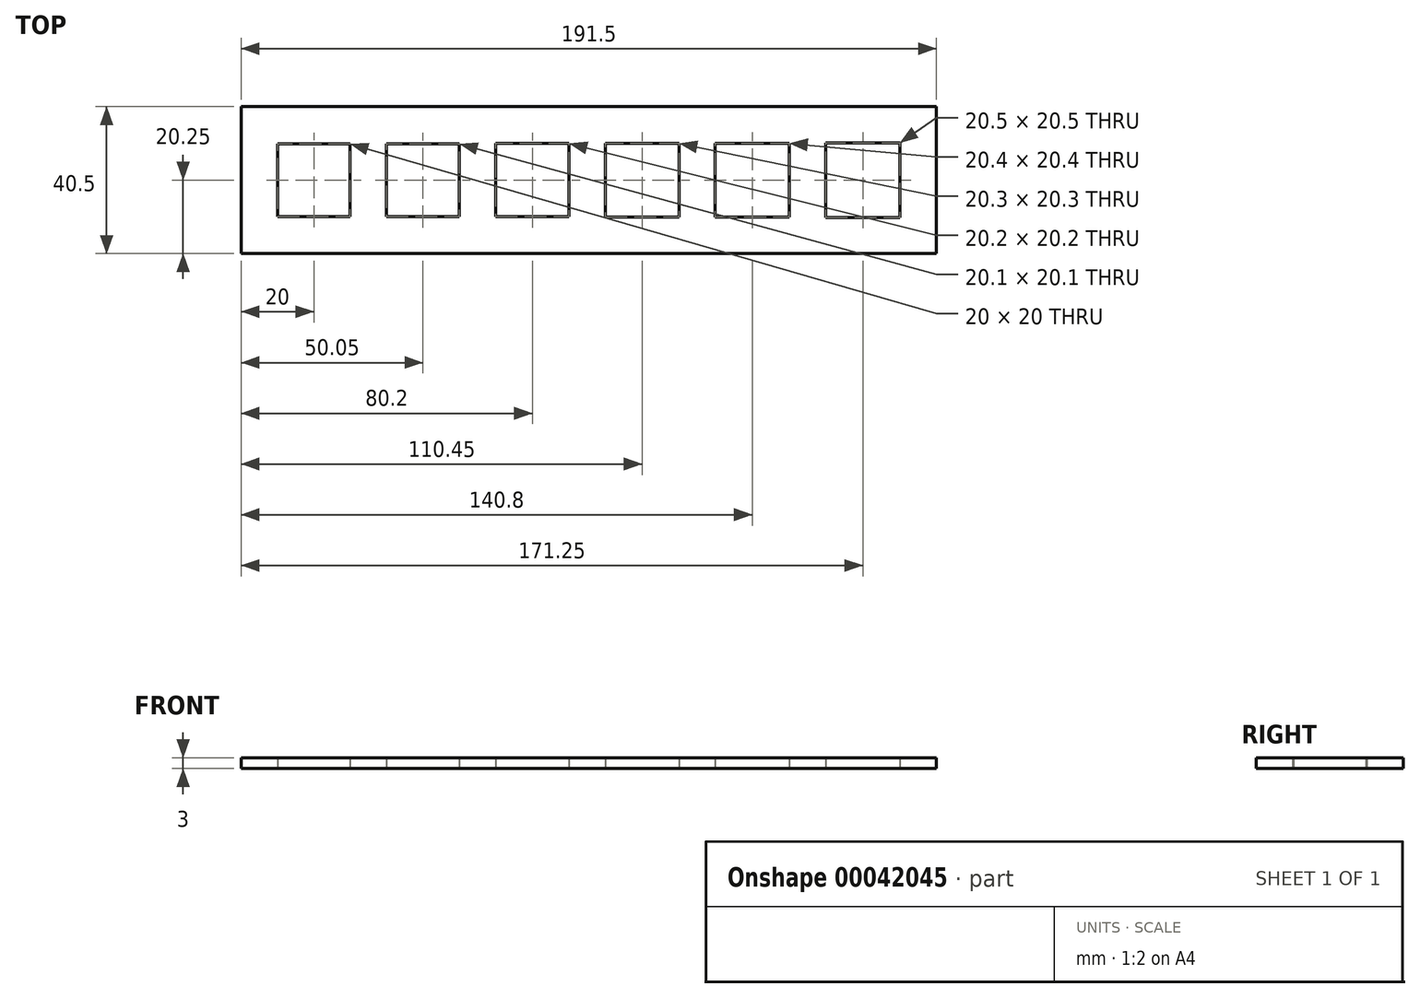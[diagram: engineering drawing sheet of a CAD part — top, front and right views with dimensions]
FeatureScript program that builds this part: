
annotation { "Feature Type Name" : "Feature", "Feature Type Description" : "" }
export const myFeature = defineFeature(function(context is Context, id is Id, definition is map)
    precondition{}
    {
        {
            var Q0;
            Q0=qCreatedBy(makeId("Top.planeOp"),FACE);
            var sketch = newSketch(context, id + "F0", { "sketchPlane" : qUnion([Q0])});
            skLineSegment(sketch, "E0.bottom", {"start": v(-95.75, 20.25) * mm, "end": v(95.75, 20.25) * mm});
            skLineSegment(sketch, "E0.top", {"start": v(-95.75, -20.25) * mm, "end": v(95.75, -20.25) * mm});
            skLineSegment(sketch, "E0.left", {"start": v(-95.75, 20.25) * mm, "end": v(-95.75, -20.25) * mm});
            skLineSegment(sketch, "E0.right", {"start": v(95.75, 20.25) * mm, "end": v(95.75, -20.25) * mm});
            skLineSegment(sketch, "E1.bottom", {"start": v(-85.75, 10) * mm, "end": v(-65.75, 10) * mm});
            skLineSegment(sketch, "E1.top", {"start": v(-85.75, -10) * mm, "end": v(-65.75, -10) * mm});
            skLineSegment(sketch, "E1.left", {"start": v(-85.75, 10) * mm, "end": v(-85.75, -10) * mm});
            skLineSegment(sketch, "E1.right", {"start": v(-65.75, 10) * mm, "end": v(-65.75, -10) * mm});
            skLineSegment(sketch, "E2.bottom", {"start": v(-55.75, 10.05) * mm, "end": v(-35.65, 10.05) * mm});
            skLineSegment(sketch, "E2.top", {"start": v(-55.75, -10.05) * mm, "end": v(-35.65, -10.05) * mm});
            skLineSegment(sketch, "E2.left", {"start": v(-55.75, 10.05) * mm, "end": v(-55.75, -10.05) * mm});
            skLineSegment(sketch, "E2.right", {"start": v(-35.65, 10.05) * mm, "end": v(-35.65, -10.05) * mm});
            skLineSegment(sketch, "E3.bottom", {"start": v(-25.65, 10.1) * mm, "end": v(-5.45, 10.1) * mm});
            skLineSegment(sketch, "E3.top", {"start": v(-25.65, -10.1) * mm, "end": v(-5.45, -10.1) * mm});
            skLineSegment(sketch, "E3.left", {"start": v(-25.65, 10.1) * mm, "end": v(-25.65, -10.1) * mm});
            skLineSegment(sketch, "E3.right", {"start": v(-5.45, 10.1) * mm, "end": v(-5.45, -10.1) * mm});
            skLineSegment(sketch, "E4.bottom", {"start": v(4.55, 10.15) * mm, "end": v(24.85, 10.15) * mm});
            skLineSegment(sketch, "E4.top", {"start": v(4.55, -10.15) * mm, "end": v(24.85, -10.15) * mm});
            skLineSegment(sketch, "E4.left", {"start": v(4.55, 10.15) * mm, "end": v(4.55, -10.15) * mm});
            skLineSegment(sketch, "E4.right", {"start": v(24.85, 10.15) * mm, "end": v(24.85, -10.15) * mm});
            skLineSegment(sketch, "E5.bottom", {"start": v(34.85, 10.2) * mm, "end": v(55.25, 10.2) * mm});
            skLineSegment(sketch, "E5.top", {"start": v(34.85, -10.2) * mm, "end": v(55.25, -10.2) * mm});
            skLineSegment(sketch, "E5.left", {"start": v(34.85, 10.2) * mm, "end": v(34.85, -10.2) * mm});
            skLineSegment(sketch, "E5.right", {"start": v(55.25, 10.2) * mm, "end": v(55.25, -10.2) * mm});
            skLineSegment(sketch, "E6.bottom", {"start": v(85.75, 10.25) * mm, "end": v(65.25, 10.25) * mm});
            skLineSegment(sketch, "E6.top", {"start": v(85.75, -10.25) * mm, "end": v(65.25, -10.25) * mm});
            skLineSegment(sketch, "E6.left", {"start": v(85.75, 10.25) * mm, "end": v(85.75, -10.25) * mm});
            skLineSegment(sketch, "E6.right", {"start": v(65.25, 10.25) * mm, "end": v(65.25, -10.25) * mm});
            skLineSegment(sketch, "E7", {"start": v(-95.75, 0) * mm, "end": v(95.75, 0) * mm, "construction": true});
            skPoint(sketch, "E8", {"position": v(-85.75, 0) * mm});
            skPoint(sketch, "E9", {"position": v(-55.75, 0) * mm});
            skPoint(sketch, "E10", {"position": v(4.55, 0) * mm});
            skPoint(sketch, "E11", {"position": v(34.85, 0) * mm});
            skPoint(sketch, "E12", {"position": v(-25.65, 0) * mm});
            skPoint(sketch, "E13", {"position": v(65.25, 0) * mm});
            skPoint(sketch, "E14", {"position": v(0, -20.25) * mm});
            skSolve(sketch);
        }
        {
            var Q0;
            Q0 = qSketchRegion(id + "F0", true);
            extrude(context, id + "F1", {"entities" : qUnion([Q0]), "depth" : 3 * mm});
        }
    });
